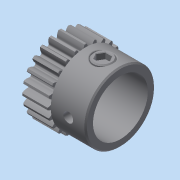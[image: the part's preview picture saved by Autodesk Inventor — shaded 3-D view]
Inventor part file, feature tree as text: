
AUTODESK INVENTOR PART (.ipt)
format: ipt  version: 2015 (Build 190159000, 159)  size: 1,102,336 bytes
history: native  units: in
note: dims shown in document units (in); Inventor stores cm internally (conversion verified against a paired STEP export)
features: imported_body x2, other x1, extrude x1, sketch x1
ambient origin geometry x8: Origin, YZ Plane, XZ Plane, XY Plane, X Axis, Y Axis, Z Axis, Center Point
bodies: Solid1 (feature_tree), Solid2 (feature_tree)
feature tree (5):
  other  "s1086z-048s0241"
  extrude  "Extrusion1"  TaperAngle=0.0deg  [1 undecoded]
  imported_body  "Base1"
  imported_body  "Base2"
  sketch  "Sketch1"  dims[d0=0.3937in d1=0.0in d2=0.0in]
note: 1 required parameter value undecoded (feature->parameter linkage not recoverable at this tier; creation-order binding heuristic only, values carry confidence <= 0.55)
